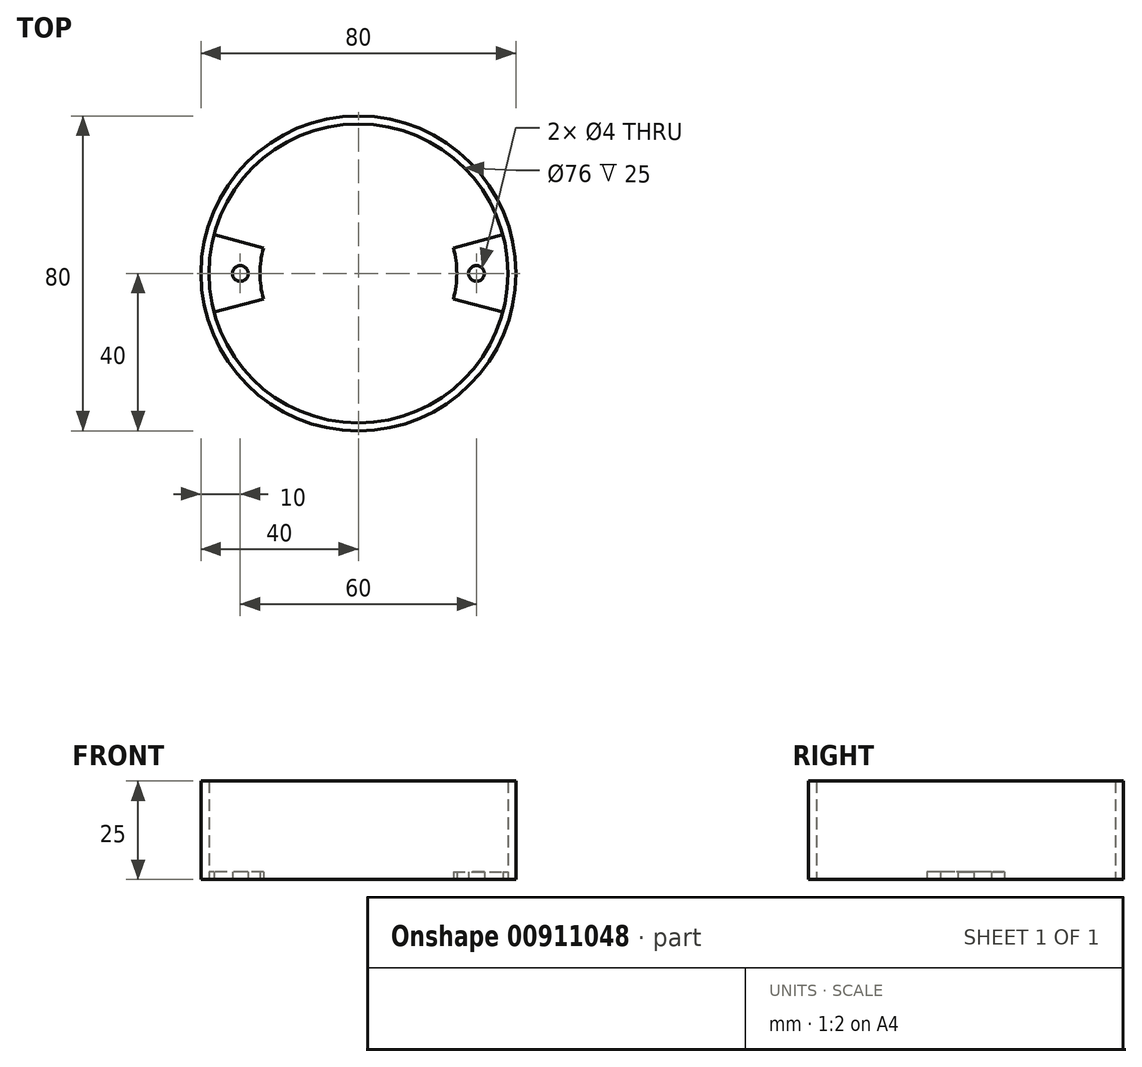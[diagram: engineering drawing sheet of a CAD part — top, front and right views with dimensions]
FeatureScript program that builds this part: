
annotation { "Feature Type Name" : "Feature", "Feature Type Description" : "" }
export const myFeature = defineFeature(function(context is Context, id is Id, definition is map)
    precondition{}
    {
        {
            var Q0;
            Q0=qCreatedBy(makeId("Top.planeOp"),FACE);
            var sketch = newSketch(context, id + "F0", { "sketchPlane" : qUnion([Q0])});
            skCircle(sketch, "E0", {"center": v(0, 0) * mm, "radius": 40 * mm});
            skCircle(sketch, "E1.0", {"center": v(0, 0) * mm, "radius": 38 * mm});
            skArc(sketch, "E2", {"start": v(24.15, -6.47) * mm, "mid": v(25, 0) * mm, "end": v(24.15, 6.47) * mm});
            skLineSegment(sketch, "E3", {"start": v(-24.15, 6.47) * mm, "end": v(-36.7, 9.84) * mm});
            skLineSegment(sketch, "E4", {"start": v(-24.15, -6.47) * mm, "end": v(-36.7, -9.84) * mm});
            skLineSegment(sketch, "E5", {"start": v(24.15, 6.47) * mm, "end": v(36.7, 9.84) * mm});
            skLineSegment(sketch, "E6", {"start": v(24.15, -6.47) * mm, "end": v(36.7, -9.84) * mm});
            skArc(sketch, "E7.trimOffspring", {"start": v(-24.15, 6.47) * mm, "mid": v(-25, 0) * mm, "end": v(-24.15, -6.47) * mm});
            skCircle(sketch, "E8", {"center": v(-30, 0) * mm, "radius": 2 * mm});
            skCircle(sketch, "E9.MirrorC", {"center": v(30, 0) * mm, "radius": 2 * mm});
            skSolve(sketch);
        }
        {
            var Q0;
            Q0 = qSketchRegion(id + "F0", true);
            extrude(context, id + "F1", {"entities" : qUnion([Q0]), "depth" : 25 * mm, "offsetDistance" : 25 * mm});
        }
        {
            var Q0;
            {var subQ0=sQuery(id+"F0.wireOp",EDGE,"E3");Q0=makeQuery(id+"F0.imprint","IMPRINT",FACE,{"disambiguationData":[TD([[makeQuery(id+"F0.imprint","IMPRINT",EDGE,{"derivedFrom":subQ0}),1.0]])]});}
            extrude(context, id + "F2", {"entities" : qUnion([Q0]), "depth" : 2 * mm, "offsetDistance" : 25 * mm});
        }
        {
            var Q0;
            Q0=makeQuery(id+"F0.imprint","IMPRINT",FACE,{"disambiguationData":[TD([[makeQuery(id+"F0.imprint","IMPRINT",EDGE,{"derivedFrom":sQuery(id+"F0.wireOp",EDGE,"E2")}),-1.0]])]});
            extrude(context, id + "F3", {"entities" : qUnion([Q0]), "depth" : 2 * mm, "offsetDistance" : 25 * mm});
        }
    });
